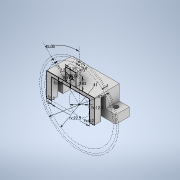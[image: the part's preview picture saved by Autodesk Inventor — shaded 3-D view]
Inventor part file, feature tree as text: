
AUTODESK INVENTOR PART (.ipt)
format: ipt  version: 2022 (Build 260153000, 153)  size: 190,976 bytes
history: native  units: mm
features: extrude x4, sketch x3, other x1
ambient origin geometry x8: Origin, YZ Plane, XZ Plane, XY Plane, X Axis, Y Axis, Z Axis, Center Point
bodies: Body1 (feature_tree)
feature tree (8):
  other  "FS90R.ipt"
  sketch  "スケッチ2"
  extrude  "ベース"  Depth=10.0mm
  extrude  "タブ切欠き"  Depth=12.1mm
  extrude  "マウント"  Depth=22.5mm
  extrude  "押し出し5"  Depth=0.2mm
  sketch  "スケッチ3"
  sketch  "スケッチ4"
